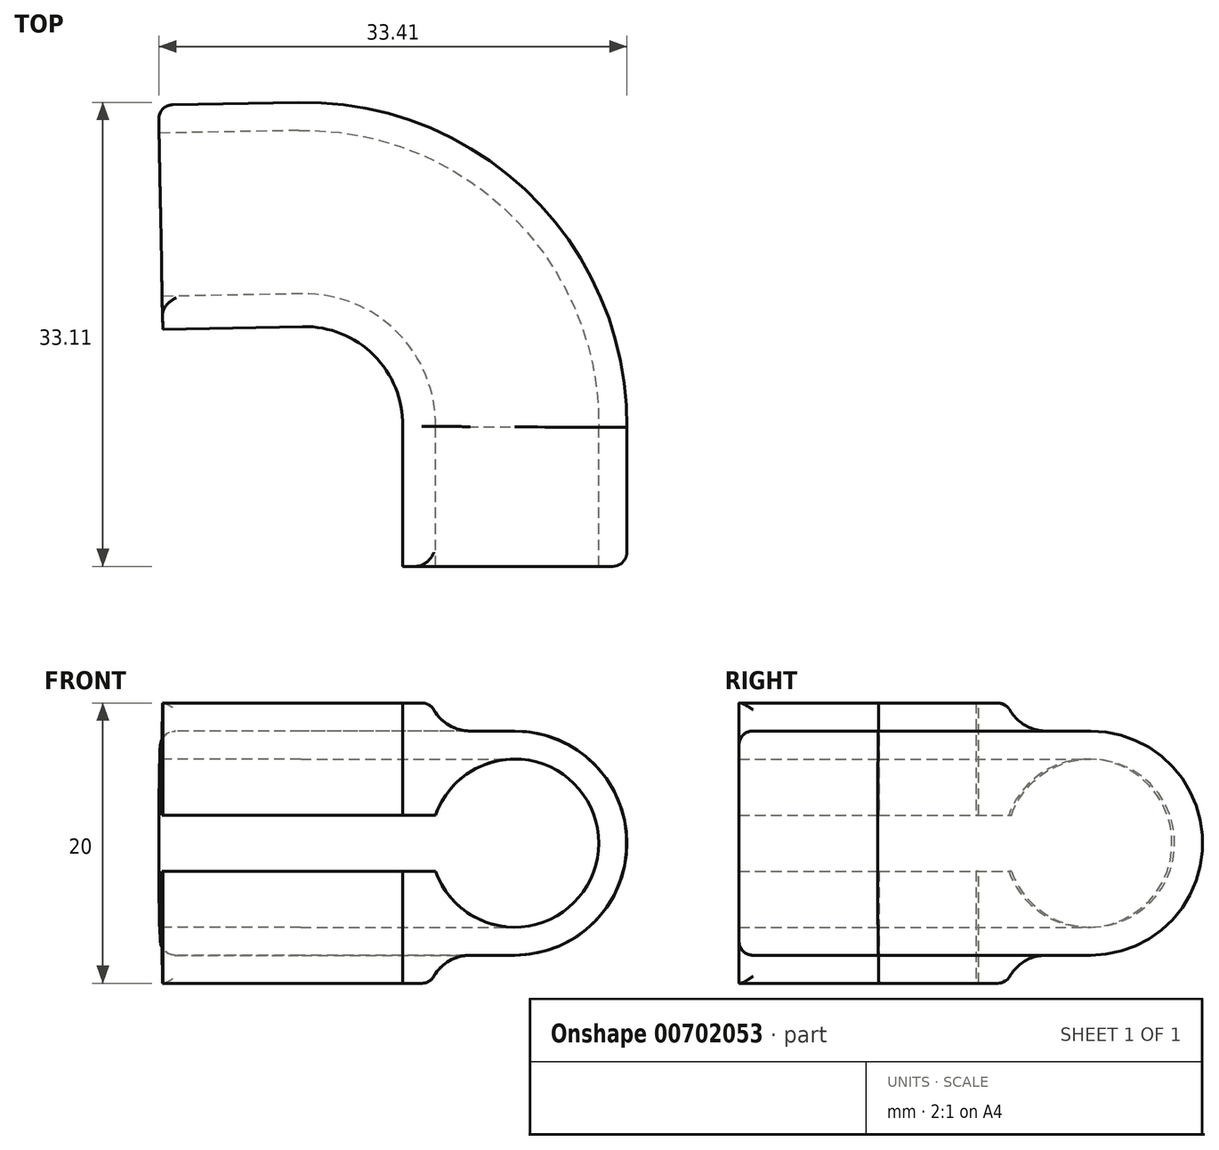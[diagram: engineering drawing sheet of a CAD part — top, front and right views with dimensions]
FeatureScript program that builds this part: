
annotation { "Feature Type Name" : "Feature", "Feature Type Description" : "" }
export const myFeature = defineFeature(function(context is Context, id is Id, definition is map)
    precondition{}
    {
        {
            var Q0;
            Q0=qCreatedBy(makeId("Top.planeOp"),FACE);
            var sketch = newSketch(context, id + "F0", { "sketchPlane" : qUnion([Q0])});
            skArc(sketch, "E0", {"start": v(7, -0.1) * mm, "mid": v(4.94, 4.96) * mm, "end": v(-0.13, 7) * mm});
            skLineSegment(sketch, "E1", {"start": v(7, -0.1) * mm, "end": v(7, -10.1) * mm});
            skLineSegment(sketch, "E2", {"start": v(-0.13, 7) * mm, "end": v(-10.13, 6.81) * mm});
            skSolve(sketch);
        }
        {
            var Q0;
            Q0=sQuery(id+"F0.wireOp",VERTEX,"E1.end");
            var Q1;
            Q1=qCreatedBy(makeId("Front.planeOp"),FACE);
            cPlane(context, id + "F1", {"entities" : qUnion([Q0, Q1]), "cplaneType" : CPlaneType.PLANE_POINT, "offset" : 25 * mm, "width" : 150 * mm, "height" : 150 * mm});
        }
        {
            var Q0;
            Q0=qCreatedBy(id+"F1.planeOp",FACE);
            var sketch = newSketch(context, id + "F2", { "sketchPlane" : qUnion([Q0])});
            skLineSegment(sketch, "E3", {"start": v(7, 10) * mm, "end": v(7, 2) * mm});
            skLineSegment(sketch, "E4", {"start": v(7, 0) * mm, "end": v(15, 0) * mm, "construction": true});
            skArc(sketch, "E5", {"start": v(15, -8) * mm, "mid": v(23, 0) * mm, "end": v(15, 8) * mm});
            skArc(sketch, "E6", {"start": v(9.34, -2) * mm, "mid": v(21, 0) * mm, "end": v(9.34, 2) * mm});
            skLineSegment(sketch, "E7", {"start": v(15, 0) * mm, "end": v(15, -8) * mm, "construction": true});
            skLineSegment(sketch, "E8.MirrorCS", {"start": v(15, 0) * mm, "end": v(15, 8) * mm, "construction": true});
            skLineSegment(sketch, "E9", {"start": v(15, -8) * mm, "end": v(9, -8) * mm});
            skLineSegment(sketch, "E10", {"start": v(7, -10) * mm, "end": v(9, -10) * mm});
            skLineSegment(sketch, "E11", {"start": v(9, -10) * mm, "end": v(9, -8) * mm});
            skLineSegment(sketch, "E12.MirrorCS", {"start": v(15, 8) * mm, "end": v(9, 8) * mm});
            skLineSegment(sketch, "E13.MirrorCS", {"start": v(9, 10) * mm, "end": v(9, 8) * mm});
            skLineSegment(sketch, "E14.MirrorCS", {"start": v(7, 10) * mm, "end": v(9, 10) * mm});
            skLineSegment(sketch, "E15.bottom", {"start": v(7, 2) * mm, "end": v(9.34, 2) * mm});
            skLineSegment(sketch, "E15.top", {"start": v(7, -2) * mm, "end": v(9.34, -2) * mm});
            skLineSegment(sketch, "E15.left", {"start": v(7, 2) * mm, "end": v(7, 0) * mm});
            skPoint(sketch, "E16.orphan", {"position": v(7, 8) * mm});
            skLineSegment(sketch, "E17.trimOffspring", {"start": v(7, -2) * mm, "end": v(7, -10) * mm});
            skPoint(sketch, "E18.orphan", {"position": v(7, -8) * mm});
            skSolve(sketch);
        }
        {
            var Q0;
            Q0=makeQuery(id+"F2.imprint","IMPRINT",FACE,{"disambiguationData":[TD([[makeQuery(id+"F2.imprint","IMPRINT",EDGE,{"derivedFrom":sQuery(id+"F2.wireOp",EDGE,"E3")}),1.0]])]});
            var Q1;
            Q1=sQuery(id+"F0.wireOp",EDGE,"E1");
            var Q2;
            Q2=sQuery(id+"F0.wireOp",EDGE,"E0");
            var Q3;
            Q3=sQuery(id+"F0.wireOp",EDGE,"E2");
            sweep(context, id + "F3", {"profiles" : qUnion([Q0]), "path" : qUnion([Q1, Q2, Q3])});
        }
        {
            var Q0;
            Q0=makeQuery(id+"F3.opSweep","SWEPT_EDGE",EDGE,{"disambiguationData":[OSD([sQuery(id+"F0.wireOp",EDGE,"E0"),sQuery(id+"F2.wireOp",EDGE,"E12.MirrorCS"),sQuery(id+"F2.wireOp",EDGE,"E13.MirrorCS")])]});
            var Q1;
            Q1=makeQuery(id+"F3.opSweep","SWEPT_EDGE",EDGE,{"disambiguationData":[OSD([sQuery(id+"F0.wireOp",EDGE,"E1"),sQuery(id+"F2.wireOp",EDGE,"E12.MirrorCS"),sQuery(id+"F2.wireOp",EDGE,"E13.MirrorCS")])]});
            var Q2;
            Q2=makeQuery(id+"F3.opSweep","SWEPT_EDGE",EDGE,{"disambiguationData":[OSD([sQuery(id+"F0.wireOp",EDGE,"E1"),sQuery(id+"F2.wireOp",EDGE,"E9"),sQuery(id+"F2.wireOp",EDGE,"E11")])]});
            fillet(context, id + "F4", {"entities" : qUnion([Q0, Q1, Q2]), "radius" : 3 * mm, "tangentPropagation" : true, "allowEdgeOverflow" : false});
        }
        {
            var Q0;
            {var subQ0=sQuery(id+"F0.wireOp",EDGE,"E1");Q0=makeQuery(id+"F4.opFillet","BLEND_EDGE",EDGE,{"disambiguationData":[OD(0.0)],"blendedFrom":[makeQuery(id+"F3.opSweep","SWEPT_EDGE",EDGE,{"disambiguationData":[OSD([subQ0,sQuery(id+"F2.wireOp",EDGE,"E9"),sQuery(id+"F2.wireOp",EDGE,"E11")])]}),makeQuery(id+"F3.opSweep","SWEPT_FACE",FACE,{"disambiguationData":[OSD([subQ0,sQuery(id+"F2.wireOp",EDGE,"E10")])]})],"blendedInto":[makeQuery(id+"F3.opSweep","SWEPT_FACE",FACE,{"disambiguationData":[OSD([subQ0,sQuery(id+"F2.wireOp",EDGE,"E10")])]})]});}
            var Q1;
            {var subQ0=sQuery(id+"F0.wireOp",EDGE,"E1");Q1=makeQuery(id+"F4.opFillet","BLEND_EDGE",EDGE,{"disambiguationData":[OD(2.0)],"blendedFrom":[makeQuery(id+"F3.opSweep","SWEPT_EDGE",EDGE,{"disambiguationData":[OSD([subQ0,sQuery(id+"F2.wireOp",EDGE,"E9"),sQuery(id+"F2.wireOp",EDGE,"E11")])]}),makeQuery(id+"F3.opSweep","SWEPT_FACE",FACE,{"disambiguationData":[OSD([subQ0,sQuery(id+"F2.wireOp",EDGE,"E10")])]})],"blendedInto":[makeQuery(id+"F3.opSweep","SWEPT_FACE",FACE,{"disambiguationData":[OSD([subQ0,sQuery(id+"F2.wireOp",EDGE,"E10")])]})]});}
            var Q2;
            {var subQ0=sQuery(id+"F0.wireOp",EDGE,"E1");Q2=makeQuery(id+"F4.opFillet","BLEND_EDGE",EDGE,{"blendedFrom":[makeQuery(id+"F3.opSweep","SWEPT_EDGE",EDGE,{"disambiguationData":[OSD([subQ0,sQuery(id+"F2.wireOp",EDGE,"E12.MirrorCS"),sQuery(id+"F2.wireOp",EDGE,"E13.MirrorCS")])]}),makeQuery(id+"F3.opSweep","SWEPT_FACE",FACE,{"disambiguationData":[OSD([subQ0,sQuery(id+"F2.wireOp",EDGE,"E14.MirrorCS")])]})],"blendedInto":[makeQuery(id+"F3.opSweep","SWEPT_FACE",FACE,{"disambiguationData":[OSD([subQ0,sQuery(id+"F2.wireOp",EDGE,"E14.MirrorCS")])]})]});}
            var Q3;
            Q3=makeQuery(id+"F4.opFillet","BLEND_EDGE",EDGE,{"blendedFrom":[makeQuery(id+"F3.opSweep","SWEPT_EDGE",EDGE,{"disambiguationData":[OSD([sQuery(id+"F0.wireOp",EDGE,"E0"),sQuery(id+"F2.wireOp",EDGE,"E12.MirrorCS"),sQuery(id+"F2.wireOp",EDGE,"E13.MirrorCS")])]}),makeQuery(id+"F3.opSweep","SWEPT_FACE",FACE,{"disambiguationData":[OSD([sQuery(id+"F0.wireOp",EDGE,"E1"),sQuery(id+"F2.wireOp",EDGE,"E14.MirrorCS")])]})],"blendedInto":[makeQuery(id+"F3.opSweep","SWEPT_FACE",FACE,{"disambiguationData":[OSD([sQuery(id+"F0.wireOp",EDGE,"E1"),sQuery(id+"F2.wireOp",EDGE,"E14.MirrorCS")])]})]});
            var Q4;
            Q4=makeQuery(id+"F3.opSweep","CAP_EDGE",EDGE,{"disambiguationData":[OSD([sQuery(id+"F0.wireOp",VERTEX,"E2.end"),sQuery(id+"F2.wireOp",EDGE,"E5")])],"isStart":false});
            var Q5;
            Q5=makeQuery(id+"F3.opSweep","CAP_EDGE",EDGE,{"disambiguationData":[OSD([sQuery(id+"F0.wireOp",VERTEX,"E1.end"),sQuery(id+"F2.wireOp",EDGE,"E5")])],"isStart":true});
            fillet(context, id + "F5", {"entities" : qUnion([Q0, Q1, Q2, Q3, Q4, Q5]), "radius" : 1 * mm, "tangentPropagation" : true, "allowEdgeOverflow" : false});
        }
    });
